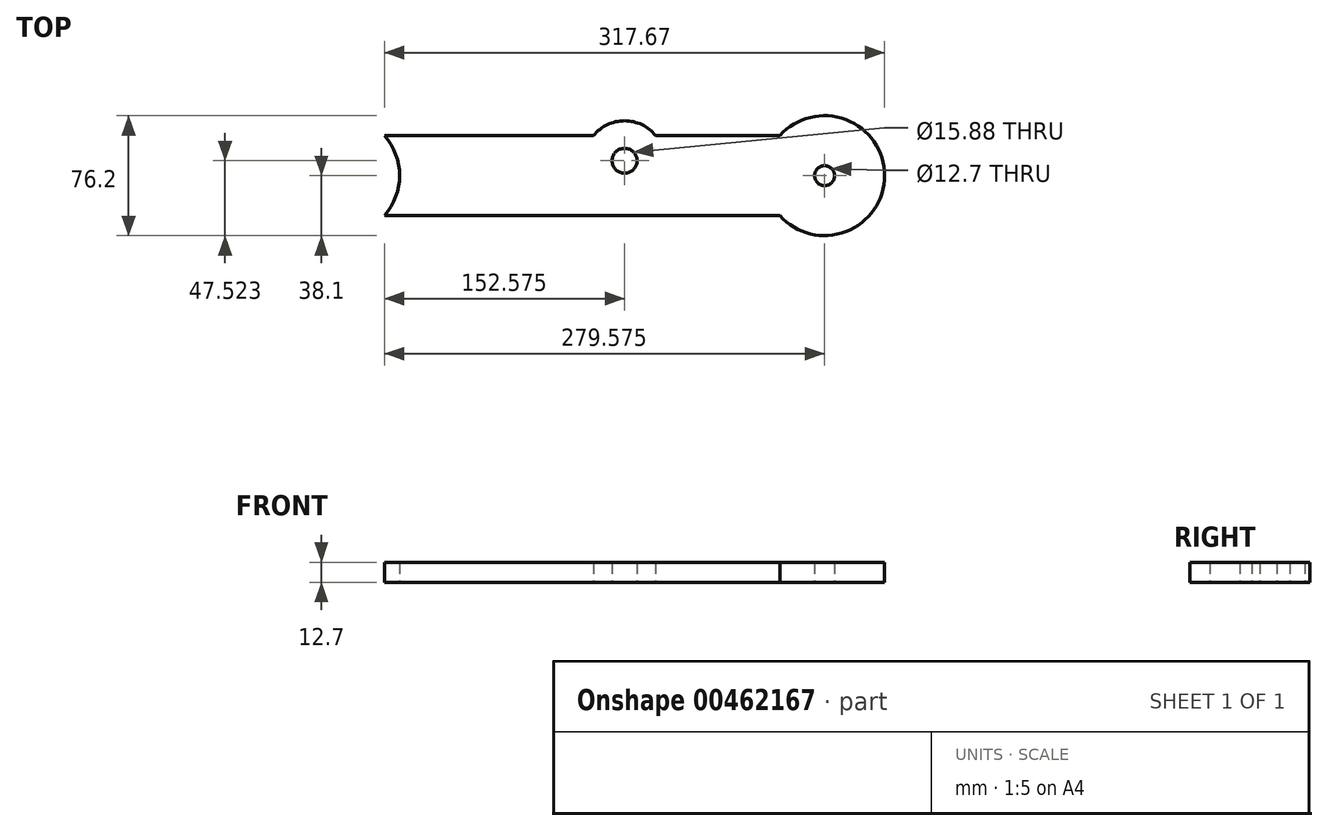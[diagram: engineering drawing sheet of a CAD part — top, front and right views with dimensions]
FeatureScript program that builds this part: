
annotation { "Feature Type Name" : "Feature", "Feature Type Description" : "" }
export const myFeature = defineFeature(function(context is Context, id is Id, definition is map)
    precondition{}
    {
        {
            var Q0;
            Q0=qCreatedBy(makeId("Top.planeOp"),FACE);
            var sketch = newSketch(context, id + "F0", { "sketchPlane" : qUnion([Q0])});
            skLineSegment(sketch, "E0.bottom", {"start": v(158.93, -25.4) * mm, "end": v(-92.25, -25.4) * mm});
            skLineSegment(sketch, "E0.top", {"start": v(158.93, 25.4) * mm, "end": v(-92.25, 25.4) * mm});
            skLineSegment(sketch, "E0.right", {"start": v(-212.73, -25.4) * mm, "end": v(-212.73, 25.4) * mm});
            skPoint(sketch, "E0.middle", {"position": v(0, 0) * mm});
            skLineSegment(sketch, "E1", {"start": v(-212.73, 0) * mm, "end": v(212.73, 0) * mm, "construction": true});
            skPoint(sketch, "E2", {"position": v(187.33, 0) * mm});
            skPoint(sketch, "E3", {"position": v(-120.65, 0) * mm});
            skPoint(sketch, "E4", {"position": v(-174.62, 0) * mm});
            skArc(sketch, "E5", {"start": v(-174.62, 38.1) * mm, "mid": v(-212.72, 0) * mm, "end": v(-174.62, -38.1) * mm});
            skCircle(sketch, "E6", {"center": v(187.33, 0) * mm, "radius": 38.1 * mm});
            skLineSegment(sketch, "E7", {"start": v(-174.62, 38.1) * mm, "end": v(-120.65, 38.1) * mm});
            skLineSegment(sketch, "E8", {"start": v(-174.62, -38.1) * mm, "end": v(-120.65, -38.1) * mm});
            skLineSegment(sketch, "E9.trimOffspring", {"start": v(-203.02, 25.4) * mm, "end": v(-212.73, 25.4) * mm});
            skArc(sketch, "E10.trimOffspring", {"start": v(-120.65, -38.1) * mm, "mid": v(-82.55, 0) * mm, "end": v(-120.65, 38.1) * mm});
            skLineSegment(sketch, "E11.trimOffspring", {"start": v(-203.02, -25.4) * mm, "end": v(-212.73, -25.4) * mm});
            skPoint(sketch, "E12.orphan", {"position": v(212.73, -25.4) * mm});
            skPoint(sketch, "E13.orphan", {"position": v(212.73, 25.4) * mm});
            skCircle(sketch, "E14", {"center": v(60.33, 9.42) * mm, "radius": 25.4 * mm});
            skCircle(sketch, "E15", {"center": v(187.33, 0) * mm, "radius": 6.35 * mm});
            skCircle(sketch, "E16", {"center": v(60.33, 9.42) * mm, "radius": 7.94 * mm});
            skCircle(sketch, "E17", {"center": v(-120.65, 0) * mm, "radius": 6.35 * mm});
            skCircle(sketch, "E18", {"center": v(-174.62, 0) * mm, "radius": 6.35 * mm});
            skSolve(sketch);
        }
        {
            var Q0;
            {var subQ5=sQuery(id+"F0.wireOp",EDGE,"E7");Q0=makeQuery(id+"F0.imprint","IMPRINT",FACE,{"disambiguationData":[TD([[makeQuery(id+"F0.imprint","IMPRINT",EDGE,{"derivedFrom":subQ5}),-1.0]])]});}
            var Q1;
            {var subQ0=sQuery(id+"F0.wireOp",EDGE,"E0.bottom");Q1=makeQuery(id+"F0.imprint","IMPRINT",FACE,{"disambiguationData":[TD([[makeQuery(id+"F0.imprint","IMPRINT",EDGE,{"derivedFrom":subQ0}),-1.0]])]});}
            var Q2;
            {var subQ0=sQuery(id+"F0.wireOp",EDGE,"E6");var subQ1=makeQuery(id+"F0.imprint","INTERSECT",VERTEX,{"derivedFrom":[sQuery(id+"F0.wireOp",EDGE,"E0.bottom"),subQ0]});Q2=makeQuery(id+"F0.imprint","IMPRINT",FACE,{"disambiguationData":[TD([[makeQuery(id+"F0.imprint","IMPRINT",EDGE,{"disambiguationData":[TD([[subQ1,1.0]])],"derivedFrom":subQ0}),1.0]])]});}
            var Q3;
            Q3=makeQuery(id+"F0.imprint","IMPRINT",FACE,{"disambiguationData":[TD([[makeQuery(id+"F0.imprint","IMPRINT",EDGE,{"derivedFrom":sQuery(id+"F0.wireOp",EDGE,"E16")}),-1.0]])]});
            var Q4;
            {var subQ0=sQuery(id+"F0.wireOp",EDGE,"E14");var subQ1=sQuery(id+"F0.wireOp",EDGE,"E0.top");var subQ2=makeQuery(id+"F0.imprint","INTERSECT",VERTEX,{"disambiguationData":[OD(0.0)],"derivedFrom":[subQ1,subQ0]});Q4=makeQuery(id+"F0.imprint","IMPRINT",FACE,{"disambiguationData":[TD([[makeQuery(id+"F0.imprint","IMPRINT",EDGE,{"disambiguationData":[TD([[subQ2,-1.0]])],"derivedFrom":subQ1}),-1.0]])]});}
            extrude(context, id + "F1", {"entities" : qUnion([Q0, Q1, Q2, Q3, Q4]), "depth" : 12.7 * mm, "symmetric" : true});
        }
        {
            var Q0;
            Q0=makeQuery(id+"F1.opExtrude","CAP_FACE",FACE,{"disambiguationData":[OSD([sQuery(id+"F0.wireOp",EDGE,"E0.bottom"),sQuery(id+"F0.wireOp",EDGE,"E0.top"),sQuery(id+"F0.wireOp",EDGE,"E5"),sQuery(id+"F0.wireOp",EDGE,"E6"),sQuery(id+"F0.wireOp",EDGE,"E7"),sQuery(id+"F0.wireOp",EDGE,"E8"),sQuery(id+"F0.wireOp",EDGE,"E10.trimOffspring"),sQuery(id+"F0.wireOp",EDGE,"E14"),sQuery(id+"F0.wireOp",EDGE,"E15"),sQuery(id+"F0.wireOp",EDGE,"E16"),sQuery(id+"F0.wireOp",EDGE,"E17"),sQuery(id+"F0.wireOp",EDGE,"E18")])],"isStart":false});
            var sketch = newSketch(context, id + "F2", { "sketchPlane" : qUnion([Q0])});
            skCircle(sketch, "E19", {"center": v(-174.62, 0) * mm, "radius": 11.11 * mm});
            skSolve(sketch);
        }
        {
            var Q0;
            Q0 = qSketchRegion(id + "F2", true);
            extrude(context, id + "F3", {"entities" : qUnion([Q0]), "operationType" : NewBodyOperationType.REMOVE, "oppositeDirection" : true, "depth" : 3.17 * mm});
        }
    });
